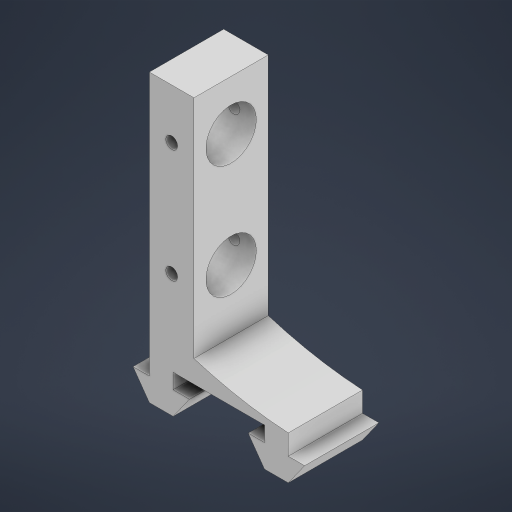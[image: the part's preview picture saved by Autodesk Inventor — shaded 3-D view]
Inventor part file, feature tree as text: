
AUTODESK INVENTOR PART (.ipt)
format: ipt  version: 2023 (Build 270158000, 158)  size: 292,352 bytes
history: native  units: mm
features: extrude x7, sketch x7, hole x1
ambient origin geometry x8: Origin, YZ Plane, XZ Plane, XY Plane, X Axis, Y Axis, Z Axis, Center Point
bodies: Solid1 (feature_tree)
feature tree (15):
  extrude  "Extrusion1"  Depth=7.75mm
  extrude  "Extrusion2"  Depth=9.5mm
  sketch  "Sketch3"  dims[d4=25.0mm d5=0.0mm d6=8.0mm]
  extrude  "Extrusion3"  Depth=8.0mm
  extrude  "Extrusion4"  Depth=6.75mm
  extrude  "Extrusion5"  Depth=10.0mm TaperAngle=0.0deg
  extrude  "Extrusion6"  Depth=25.0mm TaperAngle=0.0deg
  extrude  "Extrusion7"  Depth=2.0mm
  hole  "Hole1"  [1 undecoded]
  sketch  "Sketch1"  dims[d0=8.0mm d1=7.75mm]
  sketch  "Sketch2"  dims[d2=9.5mm d3=9.5mm]
  sketch  "Sketch4"  dims[d7=5.0mm d8=0.0mm d9=6.75mm]
  sketch  "Sketch5"  dims[d10=20.0mm d12=38.75mm d13=10.0mm d15=10.0mm d17=25.0mm d18=0.0mm]
  sketch  "Sketch6"  dims[d19=1.7mm d20=25.0mm d21=0.0mm]
  sketch  "Sketch7"  dims[d22=0.1mm d23=81.8mm d24=15.0mm d25=37.5mm d26=20.2mm d27=16.0mm d28=18.8mm d29=16.0mm d30=1.0mm d31=1.0mm d32=25.0mm d33=0.0mm d34=25.0mm d35=0.0mm d36=8.8mm d37=47.0mm d38=16.8mm d39=12.5mm d40=17.0mm d41=55.0mm d42=17.0mm d43=25.0mm d44=0.0mm d45=7.5mm d46=16.8mm d47=55.0mm d48=4.0mm d49=6.0mm d50=4.0mm d51=2.0mm d52=90.0deg d53=8.0mm d54=20.594885mm]
note: 1 required parameter value undecoded (feature->parameter linkage not recoverable at this tier; creation-order binding heuristic only, values carry confidence <= 0.55)
